# Revit family: RL-1 Rücklaufventil Eck 3724
name_source: partatom
category: Rohrzubehör
units: mm (PartAtom-declared; Revit-internal decimal feet)

## family parameters
Arbeitsebenenbasiert = Nein
Beim Laden mit Abzugskörper schneiden = Nein
Bemaßung runder Anschluss = Durchmesser verwenden
Gemeinsam genutzt = Nein
Immer vertikal = Nein
OmniClass-Nummer = 23.65.55.14
OmniClass-Titel = Valves for Liquid Services
Teiletyp = Unterbricht

## types (1)
- RL-1 Rücklaufventil Eck 3724
    Anwendungsgebiet = Warmwasserheizungsanlagen.
Durch Einbau des Rücklaufventils ist der Heizkörper-Rücklaufanschluß absperrbar.
Dadurch kann bei gleichzeitiger Absperrung des Vorlaufventils der Heizkörper bei unter Druck stehender Anlage demontiert werden.
Es ist dann möglich, Servicearbeiten oder Arbeiten an der Wand hinter dem Heizkörper (Tapezierung, Verfl iesung) durchzuführen, ohne die übrige Anlage stillsetzen zu müssen.
Ist eine Voreinstellung des Rücklaufventils oder Füllen und Entleeren von Heizkörper oder Anlage über das Rücklaufventil gefordert, wird der Einbau des Rücklaufventils HERZ-RL-5 empfohlen.
    Ausführungen = Alle Modelle werden in vernickelter Ausführung geliefert und sind Universalmodelle mit Spezialmuffe für
Gewinderohr und Klemmsetanschluß.
    Gehäuse = vernickeltes Messing
    H04 = 25.5 mm
    H05 = 5.2 mm  [stored 0.0170604 ft]
    Hersteller = HERZ Armaturen Ges.m.b.H.
    Max.Betriebsdruck = 1000000.0 Pa
    Max.Betriebstemperatur = 120 °C
    Medium = Heizwasserqualität entsprechend ÖNORM H 5195 bzw. VDI-Richtllinie 2035.
    R01 = 10.5 mm  [stored 0.0344488 ft]
    R06 = 11 mm  [stored 0.0360892 ft]
    S01 = 10 mm  [stored 0.0328084 ft]
    S04 = 45 mm  [stored 0.147638 ft]
    SCRNCODE = 05;01;02
    SCRNSEQ = ARM;ARM_TYP="ALLF";2
    URL = www.herz-armaturen.at
    Vorgabe-Ansicht = 0 mm  [stored 0 ft]

note: [stored X ft] marks values corroborated as IEEE doubles in the binary element streams (Revit-internal decimal feet)
